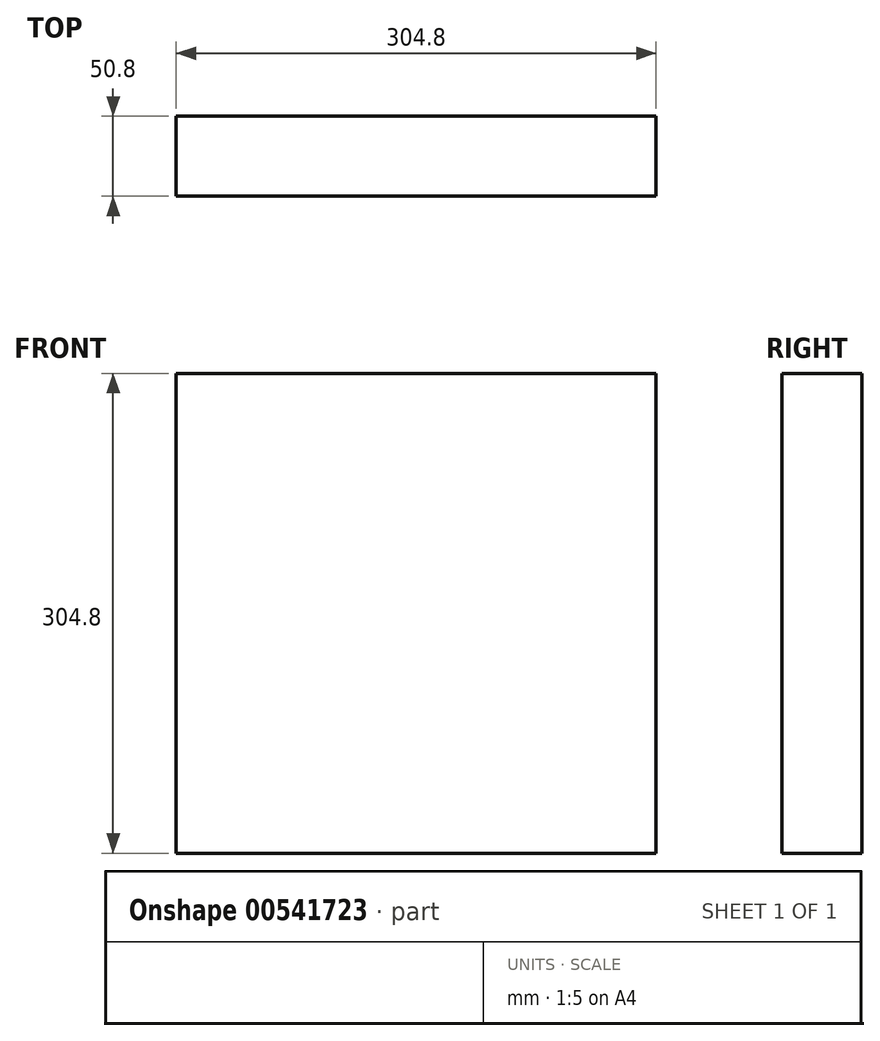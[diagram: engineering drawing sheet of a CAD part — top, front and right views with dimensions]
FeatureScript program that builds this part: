
annotation { "Feature Type Name" : "Feature", "Feature Type Description" : "" }
export const myFeature = defineFeature(function(context is Context, id is Id, definition is map)
    precondition{}
    {
        {
            var Q0;
            Q0=qCreatedBy(makeId("Top.planeOp"),FACE);
            var sketch = newSketch(context, id + "F0", { "sketchPlane" : qUnion([Q0])});
            skLineSegment(sketch, "E0.bottom", {"start": v(0, 0) * mm, "end": v(304.8, 0) * mm});
            skLineSegment(sketch, "E0.top", {"start": v(0, -50.8) * mm, "end": v(304.8, -50.8) * mm});
            skLineSegment(sketch, "E0.left", {"start": v(0, 0) * mm, "end": v(0, -50.8) * mm});
            skLineSegment(sketch, "E0.right", {"start": v(304.8, 0) * mm, "end": v(304.8, -50.8) * mm});
            skSolve(sketch);
        }
        {
            var Q0;
            Q0 = qSketchRegion(id + "F0", true);
            extrude(context, id + "F1", {"entities" : qUnion([Q0]), "depth" : 304.8 * mm, "offsetDistance" : 25.4 * mm});
        }
    });
